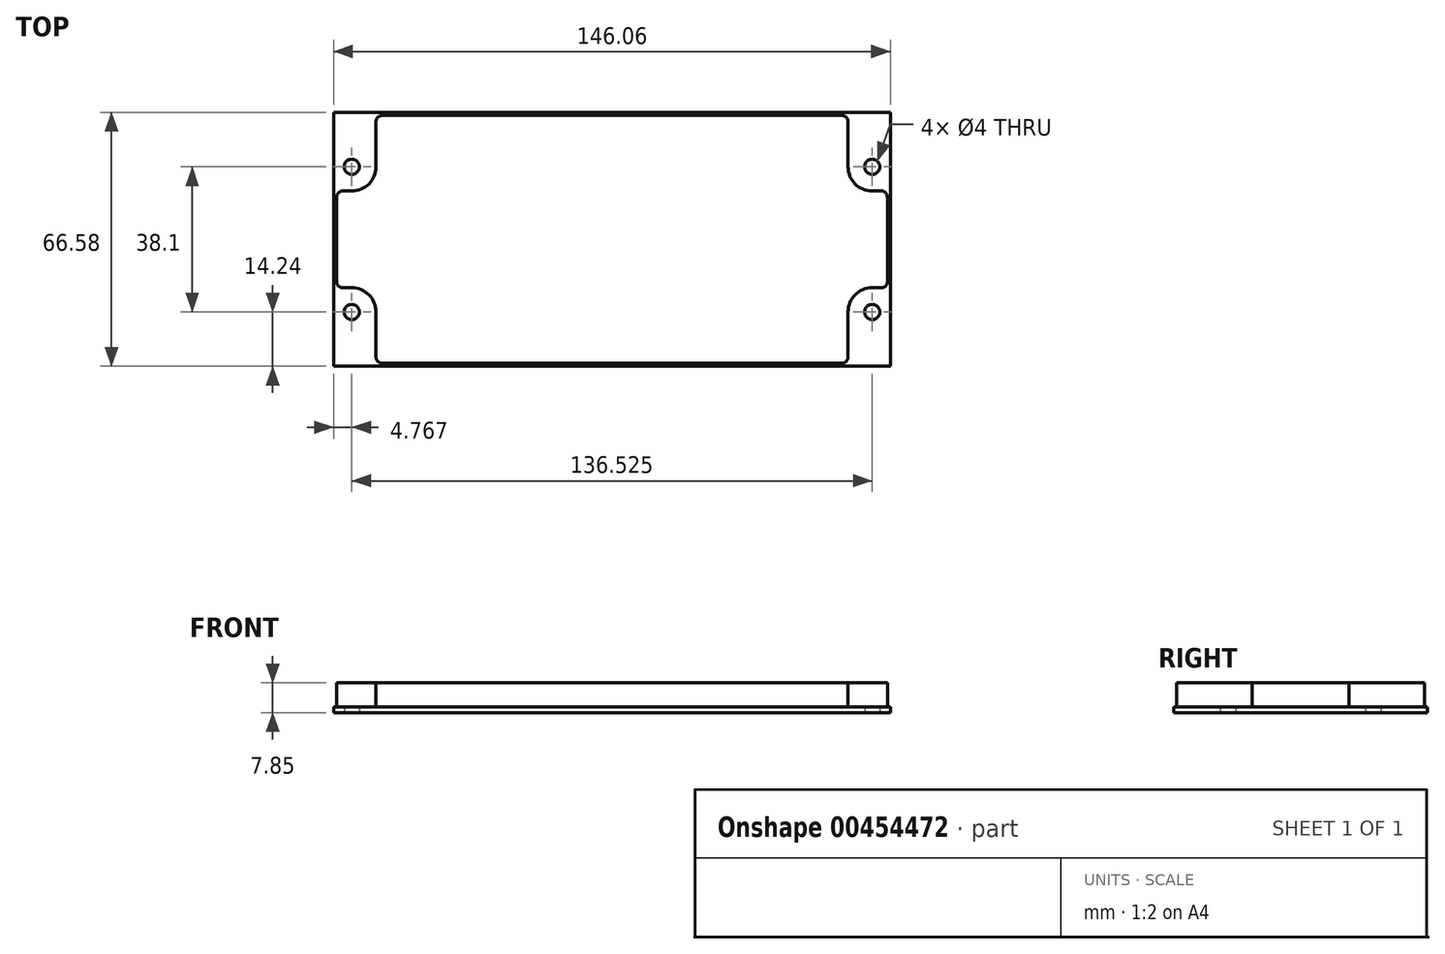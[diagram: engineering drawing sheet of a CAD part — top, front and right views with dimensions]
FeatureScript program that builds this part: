
annotation { "Feature Type Name" : "Feature", "Feature Type Description" : "" }
export const myFeature = defineFeature(function(context is Context, id is Id, definition is map)
    precondition{}
    {
        {
            var Q0;
            Q0=qCreatedBy(makeId("Top.planeOp"),FACE);
            var sketch = newSketch(context, id + "F0", { "sketchPlane" : qUnion([Q0])});
            skLineSegment(sketch, "E0.bottom", {"start": v(-73.03, 33.29) * mm, "end": v(73.03, 33.29) * mm, "construction": true});
            skLineSegment(sketch, "E0.top", {"start": v(-73.03, -33.29) * mm, "end": v(73.03, -33.29) * mm, "construction": true});
            skLineSegment(sketch, "E0.left", {"start": v(-73.02, 33.29) * mm, "end": v(-73.03, -33.29) * mm, "construction": true});
            skLineSegment(sketch, "E0.right", {"start": v(73.03, 33.29) * mm, "end": v(73.03, -33.29) * mm, "construction": true});
            skCircle(sketch, "E1", {"center": v(-68.26, -19.05) * mm, "radius": 4.76 * mm});
            skCircle(sketch, "E2", {"center": v(-68.26, 19.05) * mm, "radius": 4.76 * mm});
            skPoint(sketch, "E3.third.point.positionSnap0", {"position": v(73.03, 0) * mm});
            skCircle(sketch, "E4", {"center": v(68.26, 19.05) * mm, "radius": 4.76 * mm});
            skCircle(sketch, "E5", {"center": v(68.26, -19.05) * mm, "radius": 4.76 * mm});
            skPoint(sketch, "E6", {"position": v(0, 33.29) * mm});
            skLineSegment(sketch, "E7.bottom", {"start": v(-73.03, 33.29) * mm, "end": v(73.03, 33.29) * mm});
            skLineSegment(sketch, "E7.top", {"start": v(-73.03, -33.29) * mm, "end": v(73.03, -33.29) * mm});
            skLineSegment(sketch, "E7.left", {"start": v(-73.03, 33.29) * mm, "end": v(-73.03, -33.29) * mm});
            skLineSegment(sketch, "E7.right", {"start": v(73.03, 33.29) * mm, "end": v(73.03, -33.29) * mm});
            skCircle(sketch, "E8", {"center": v(-68.26, 19.05) * mm, "radius": 2 * mm});
            skCircle(sketch, "E9", {"center": v(68.26, -19.05) * mm, "radius": 2 * mm});
            skCircle(sketch, "E10", {"center": v(-68.26, -19.05) * mm, "radius": 2 * mm});
            skCircle(sketch, "E11", {"center": v(68.26, 19.05) * mm, "radius": 2 * mm});
            skArc(sketch, "E12", {"start": v(68.26, 25.4) * mm, "mid": v(61.91, 19.05) * mm, "end": v(68.26, 12.7) * mm});
            skArc(sketch, "E13", {"start": v(68.26, -12.7) * mm, "mid": v(61.91, -19.05) * mm, "end": v(68.26, -25.4) * mm});
            skArc(sketch, "E14", {"start": v(-68.26, -25.4) * mm, "mid": v(-61.91, -19.05) * mm, "end": v(-68.26, -12.7) * mm});
            skArc(sketch, "E15", {"start": v(-68.26, 12.7) * mm, "mid": v(-61.91, 19.05) * mm, "end": v(-68.26, 25.4) * mm});
            skLineSegment(sketch, "E16", {"start": v(68.26, 25.4) * mm, "end": v(73.02, 25.4) * mm});
            skLineSegment(sketch, "E17", {"start": v(68.26, 12.7) * mm, "end": v(73.02, 12.7) * mm});
            skLineSegment(sketch, "E18", {"start": v(68.26, -12.7) * mm, "end": v(73.02, -12.7) * mm});
            skLineSegment(sketch, "E19", {"start": v(68.26, -25.4) * mm, "end": v(73.02, -25.4) * mm});
            skLineSegment(sketch, "E20", {"start": v(-68.26, -12.7) * mm, "end": v(-73.03, -12.7) * mm});
            skLineSegment(sketch, "E21", {"start": v(-68.26, -25.4) * mm, "end": v(-73.03, -25.4) * mm});
            skLineSegment(sketch, "E22", {"start": v(-68.26, 25.4) * mm, "end": v(-73.03, 25.4) * mm});
            skLineSegment(sketch, "E23", {"start": v(-68.26, 12.7) * mm, "end": v(-73.03, 12.7) * mm});
            skLineSegment(sketch, "E24", {"start": v(61.91, 19.05) * mm, "end": v(61.91, 33.29) * mm});
            skLineSegment(sketch, "E25", {"start": v(61.91, 33.29) * mm, "end": v(61.91, 27) * mm});
            skSolve(sketch);
        }
        {
            var Q0;
            {var subQ3=sQuery(id+"F0.wireOp",EDGE,"E7.bottom");Q0=makeQuery(id+"F0.imprint","IMPRINT",FACE,{"disambiguationData":[TD([[makeQuery(id+"F0.imprint","IMPRINT",EDGE,{"derivedFrom":subQ3}),-1.0]])]});}
            var Q1;
            {var subQ2=sQuery(id+"F0.wireOp",EDGE,"E2");Q1=makeQuery(id+"F0.imprint","IMPRINT",FACE,{"disambiguationData":[TD([[makeQuery(id+"F0.imprint","IMPRINT",EDGE,{"derivedFrom":subQ2}),-1.0]])]});}
            var Q2;
            Q2=makeQuery(id+"F0.imprint","IMPRINT",FACE,{"disambiguationData":[TD([[makeQuery(id+"F0.imprint","IMPRINT",EDGE,{"derivedFrom":sQuery(id+"F0.wireOp",EDGE,"E2")}),1.0]])]});
            var Q3;
            {var subQ2=sQuery(id+"F0.wireOp",EDGE,"E1");Q3=makeQuery(id+"F0.imprint","IMPRINT",FACE,{"disambiguationData":[TD([[makeQuery(id+"F0.imprint","IMPRINT",EDGE,{"derivedFrom":subQ2}),-1.0]])]});}
            var Q4;
            Q4=makeQuery(id+"F0.imprint","IMPRINT",FACE,{"disambiguationData":[TD([[makeQuery(id+"F0.imprint","IMPRINT",EDGE,{"derivedFrom":sQuery(id+"F0.wireOp",EDGE,"E1")}),1.0]])]});
            var Q5;
            {var subQ2=sQuery(id+"F0.wireOp",EDGE,"E4");Q5=makeQuery(id+"F0.imprint","IMPRINT",FACE,{"disambiguationData":[TD([[makeQuery(id+"F0.imprint","IMPRINT",EDGE,{"derivedFrom":subQ2}),-1.0]])]});}
            var Q6;
            Q6=makeQuery(id+"F0.imprint","IMPRINT",FACE,{"disambiguationData":[TD([[makeQuery(id+"F0.imprint","IMPRINT",EDGE,{"derivedFrom":sQuery(id+"F0.wireOp",EDGE,"E4")}),1.0]])]});
            var Q7;
            {var subQ0=sQuery(id+"F0.wireOp",EDGE,"E5");Q7=makeQuery(id+"F0.imprint","IMPRINT",FACE,{"disambiguationData":[TD([[makeQuery(id+"F0.imprint","IMPRINT",EDGE,{"derivedFrom":subQ0}),-1.0]])]});}
            var Q8;
            Q8=makeQuery(id+"F0.imprint","IMPRINT",FACE,{"disambiguationData":[TD([[makeQuery(id+"F0.imprint","IMPRINT",EDGE,{"derivedFrom":sQuery(id+"F0.wireOp",EDGE,"E5")}),1.0]])]});
            var Q9;
            {var subQ5=sQuery(id+"F0.wireOp",EDGE,"E7.top");Q9=makeQuery(id+"F0.imprint","IMPRINT",FACE,{"disambiguationData":[TD([[makeQuery(id+"F0.imprint","IMPRINT",EDGE,{"derivedFrom":subQ5}),1.0]])]});}
            extrude(context, id + "F1", {"entities" : qUnion([Q0, Q1, Q2, Q3, Q4, Q5, Q6, Q7, Q8, Q9]), "depth" : 1.5 * mm});
        }
        {
            var Q0;
            Q0=makeQuery(id+"F1.opExtrude","CAP_FACE",FACE,{"disambiguationData":[OSD([sQuery(id+"F0.wireOp",EDGE,"E7.bottom"),sQuery(id+"F0.wireOp",EDGE,"E7.top"),sQuery(id+"F0.wireOp",EDGE,"E7.left"),sQuery(id+"F0.wireOp",EDGE,"E7.right"),sQuery(id+"F0.wireOp",EDGE,"E8"),sQuery(id+"F0.wireOp",EDGE,"E9"),sQuery(id+"F0.wireOp",EDGE,"E10"),sQuery(id+"F0.wireOp",EDGE,"E11")])],"isStart":false});
            var sketch = newSketch(context, id + "F2", { "sketchPlane" : qUnion([Q0])});
            skLineSegment(sketch, "E26.0", {"start": v(68.26, 12.7) * mm, "end": v(70.64, 12.7) * mm});
            skArc(sketch, "E26.1", {"start": v(68.26, 25.4) * mm, "mid": v(61.91, 19.05) * mm, "end": v(68.26, 12.7) * mm});
            skLineSegment(sketch, "E26.2", {"start": v(68.26, 25.4) * mm, "end": v(70.64, 25.4) * mm});
            skLineSegment(sketch, "E27.0", {"start": v(73.03, 33.29) * mm, "end": v(73.03, -33.29) * mm});
            skLineSegment(sketch, "E27.1", {"start": v(68.26, -12.7) * mm, "end": v(70.64, -12.7) * mm});
            skArc(sketch, "E27.2", {"start": v(68.26, -12.7) * mm, "mid": v(61.91, -19.05) * mm, "end": v(68.26, -25.4) * mm});
            skLineSegment(sketch, "E27.3", {"start": v(68.26, -25.4) * mm, "end": v(70.64, -25.4) * mm});
            skLineSegment(sketch, "E27.4", {"start": v(-73.03, -33.29) * mm, "end": v(73.03, -33.29) * mm});
            skLineSegment(sketch, "E27.5", {"start": v(-73.03, 33.29) * mm, "end": v(-73.03, -33.29) * mm});
            skLineSegment(sketch, "E27.6", {"start": v(-68.26, -25.4) * mm, "end": v(-70.64, -25.4) * mm});
            skArc(sketch, "E27.7", {"start": v(-68.26, -25.4) * mm, "mid": v(-61.91, -19.05) * mm, "end": v(-68.26, -12.7) * mm});
            skLineSegment(sketch, "E27.8", {"start": v(-68.26, -12.7) * mm, "end": v(-70.64, -12.7) * mm});
            skLineSegment(sketch, "E27.9", {"start": v(-73.03, 33.29) * mm, "end": v(73.03, 33.29) * mm});
            skArc(sketch, "E27.10", {"start": v(-68.26, 12.7) * mm, "mid": v(-61.91, 19.05) * mm, "end": v(-68.26, 25.4) * mm});
            skLineSegment(sketch, "E27.11", {"start": v(-68.26, 12.7) * mm, "end": v(-70.64, 12.7) * mm});
            skLineSegment(sketch, "E27.12", {"start": v(-68.26, 25.4) * mm, "end": v(-70.64, 25.4) * mm});
            skLineSegment(sketch, "E28.0", {"start": v(-60.32, 32.49) * mm, "end": v(60.32, 32.49) * mm});
            skLineSegment(sketch, "E28.1", {"start": v(-72.22, 30.9) * mm, "end": v(-72.22, 26.99) * mm});
            skLineSegment(sketch, "E28.2", {"start": v(-60.32, -32.49) * mm, "end": v(60.32, -32.49) * mm});
            skLineSegment(sketch, "E28.3", {"start": v(72.23, 30.9) * mm, "end": v(72.23, 26.99) * mm});
            skPoint(sketch, "E29", {"position": v(-72.23, 12.7) * mm});
            skPoint(sketch, "E30", {"position": v(-72.22, 25.4) * mm});
            skPoint(sketch, "E31", {"position": v(-72.23, -12.7) * mm});
            skPoint(sketch, "E32", {"position": v(-72.23, -25.4) * mm});
            skPoint(sketch, "E33", {"position": v(72.23, -25.4) * mm});
            skPoint(sketch, "E34", {"position": v(72.23, -12.7) * mm});
            skPoint(sketch, "E35", {"position": v(72.23, 25.4) * mm});
            skPoint(sketch, "E36", {"position": v(72.23, 12.7) * mm});
            skLineSegment(sketch, "E37.trimOffspring", {"start": v(72.23, 11.11) * mm, "end": v(72.23, -11.11) * mm});
            skPoint(sketch, "E38.orphan", {"position": v(73.02, 25.4) * mm});
            skPoint(sketch, "E39.orphan", {"position": v(73.02, 12.7) * mm});
            skLineSegment(sketch, "E40.trimOffspring", {"start": v(72.23, -26.99) * mm, "end": v(72.23, -30.9) * mm});
            skPoint(sketch, "E41.orphan", {"position": v(73.02, -25.4) * mm});
            skPoint(sketch, "E42.orphan", {"position": v(73.02, -12.7) * mm});
            skLineSegment(sketch, "E43.trimOffspring", {"start": v(-72.23, -26.99) * mm, "end": v(-72.23, -30.9) * mm});
            skPoint(sketch, "E44.orphan", {"position": v(-73.03, -25.4) * mm});
            skPoint(sketch, "E45.orphan", {"position": v(-73.03, -12.7) * mm});
            skPoint(sketch, "E46.orphan", {"position": v(-73.03, 25.4) * mm});
            skLineSegment(sketch, "E47.trimOffspring", {"start": v(-72.23, 11.11) * mm, "end": v(-72.23, -11.11) * mm});
            skPoint(sketch, "E48.orphan", {"position": v(-73.03, 12.7) * mm});
            skArc(sketch, "E49.filletArc", {"start": v(-72.22, 26.99) * mm, "mid": v(-71.76, 25.87) * mm, "end": v(-70.64, 25.4) * mm});
            skArc(sketch, "E50.filletArc", {"start": v(-70.64, 12.7) * mm, "mid": v(-71.76, 12.23) * mm, "end": v(-72.23, 11.11) * mm});
            skPoint(sketch, "E51.visualSharp", {"position": v(-72.22, 32.49) * mm});
            skArc(sketch, "E51.filletArc", {"start": v(-70.64, 32.49) * mm, "mid": v(-71.76, 32.02) * mm, "end": v(-72.22, 30.9) * mm});
            skArc(sketch, "E52.filletArc", {"start": v(-72.23, -11.11) * mm, "mid": v(-71.76, -12.23) * mm, "end": v(-70.64, -12.7) * mm});
            skArc(sketch, "E53.filletArc", {"start": v(-70.64, -25.4) * mm, "mid": v(-71.76, -25.87) * mm, "end": v(-72.23, -26.99) * mm});
            skPoint(sketch, "E54.visualSharp", {"position": v(-72.23, -32.49) * mm});
            skArc(sketch, "E54.filletArc", {"start": v(-72.23, -30.9) * mm, "mid": v(-71.76, -32.02) * mm, "end": v(-70.64, -32.49) * mm});
            skPoint(sketch, "E55.visualSharp", {"position": v(72.23, -32.49) * mm});
            skArc(sketch, "E55.filletArc", {"start": v(70.64, -32.49) * mm, "mid": v(71.76, -32.02) * mm, "end": v(72.23, -30.9) * mm});
            skArc(sketch, "E56.filletArc", {"start": v(72.23, -26.99) * mm, "mid": v(71.76, -25.87) * mm, "end": v(70.64, -25.4) * mm});
            skArc(sketch, "E57.filletArc", {"start": v(70.64, -12.7) * mm, "mid": v(71.76, -12.23) * mm, "end": v(72.23, -11.11) * mm});
            skArc(sketch, "E58.filletArc", {"start": v(72.23, 11.11) * mm, "mid": v(71.76, 12.23) * mm, "end": v(70.64, 12.7) * mm});
            skArc(sketch, "E59.filletArc", {"start": v(70.64, 25.4) * mm, "mid": v(71.76, 25.87) * mm, "end": v(72.23, 26.99) * mm});
            skPoint(sketch, "E60.visualSharp", {"position": v(72.23, 32.49) * mm});
            skArc(sketch, "E60.filletArc", {"start": v(72.23, 30.9) * mm, "mid": v(71.76, 32.02) * mm, "end": v(70.64, 32.49) * mm});
            skLineSegment(sketch, "E61", {"start": v(61.91, 19.05) * mm, "end": v(61.91, 30.9) * mm});
            skLineSegment(sketch, "E62", {"start": v(61.91, -19.05) * mm, "end": v(61.91, -30.9) * mm});
            skLineSegment(sketch, "E63", {"start": v(-61.91, 19.05) * mm, "end": v(-61.91, 30.9) * mm});
            skLineSegment(sketch, "E64", {"start": v(-61.91, -19.05) * mm, "end": v(-61.91, -30.9) * mm});
            skArc(sketch, "E65.filletArc", {"start": v(-60.32, 32.49) * mm, "mid": v(-61.45, 32.02) * mm, "end": v(-61.91, 30.9) * mm});
            skArc(sketch, "E66.filletArc", {"start": v(-61.91, -30.9) * mm, "mid": v(-61.45, -32.02) * mm, "end": v(-60.32, -32.49) * mm});
            skArc(sketch, "E67.filletArc", {"start": v(60.32, -32.49) * mm, "mid": v(61.45, -32.02) * mm, "end": v(61.91, -30.9) * mm});
            skArc(sketch, "E68.filletArc", {"start": v(61.91, 30.9) * mm, "mid": v(61.45, 32.02) * mm, "end": v(60.32, 32.49) * mm});
            skSolve(sketch);
        }
        {
            var Q0;
            Q0=makeQuery(id+"F2.imprint","IMPRINT",FACE,{"disambiguationData":[TD([[makeQuery(id+"F2.imprint","IMPRINT",EDGE,{"derivedFrom":sQuery(id+"F2.wireOp",EDGE,"E26.0")}),-1.0]])]});
            extrude(context, id + "F3", {"entities" : qUnion([Q0]), "depth" : 6.35 * mm});
        }
    });
